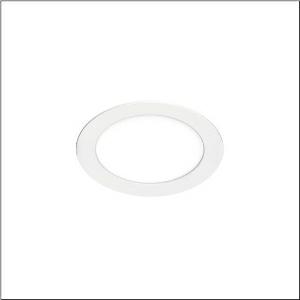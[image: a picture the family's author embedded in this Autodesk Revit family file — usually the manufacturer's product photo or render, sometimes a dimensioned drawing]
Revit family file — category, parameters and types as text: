
# Revit family: lunis_41_flat_51dr10mfgcb
name_source: partatom
category: Lighting Fixtures
units: mm (PartAtom-declared; Revit-internal decimal feet)

## family parameters
Cut with Voids When Loaded = No
Host = Face
Light Source = No
Part Type = Normal
Room Calculation Point = No
Round Connector Dimension = Use Diameter
Shared = No

## types (1)
- --- (1 x LED, 2430 lm, 19.5 W, 4000K)
    Apparent Load = 20 VA
    CIE Flux Codes = 49 80 96 100 100
    Color Rendering = 80
    Color Temperature = 4000K
    Default Elevation = 1800 mm
    Description = Lunis 41,  Flat, downlight, light emission: direct distribution, LED rated luminous flux: 2.360lm, light colour: 830/840, mains connection: 230V, AC, 50/60Hz, housing, round, of aluminium, coated, traffic white (RAL 9016), diameter: 225mm, protection rating (complete): IP20, protection rating (on room side): IP44, insulation class (complete): insulation class II (safety insulation), certification: CE, permissible ambient temperature for indoor applications: -20..+40°C, packaging unit: 1 piece
    Height = 0 mm  [stored 0 ft]
    Lamp = 1 x LED
    Lamp Light Flux = 2430 lm
    Lamp Power = 19.5 W
    Lamp count = 1
    Length = 225 mm
    Luminous efficacy = 125 lm/W
    Manufacturer = Siteco
    ModVariant = No
    Model = 51DR10MFGCB
    Mounting Place = Ceiling
    Mounting Type = Recessed
    Number of Poles = 1
    OnlyDefault = Yes
    Power Factor = 1
    Product Name = Lunis 41 Flat
    Product group = downlight
    ProductGroupID = 401
    Protection Class = Protection class II
    Protection Degree = IP 20
    RLX_Detail_Level = 1
    RLX_Emergency_Light_Flux = 0 lm
    RLX_Emergency_Type = 0
    RLX_Emergency_Type_DB = No
    RlxData = <blob elided: 11581 chars, md5=7f344777>
    Socket = socket
    Standby Power = 0 W
    System Light Flux = 2430 lm
    System Power = 20 W
    Type Comments = factory setting: colour temperature 4000K
    Type Image = l_1340923.jpg
    URL = http://relux.com
    VarID = @adj_018939
    Voltage = 0 V
    Weight = 0.00 kg
    Width = 0 mm  [stored 0 ft]

note: [stored X ft] marks values corroborated as IEEE doubles in the binary element streams (Revit-internal decimal feet)

## geometry (parser evidence)
native form markers: Sweep x8
no freeform markers — native parametric forms only
